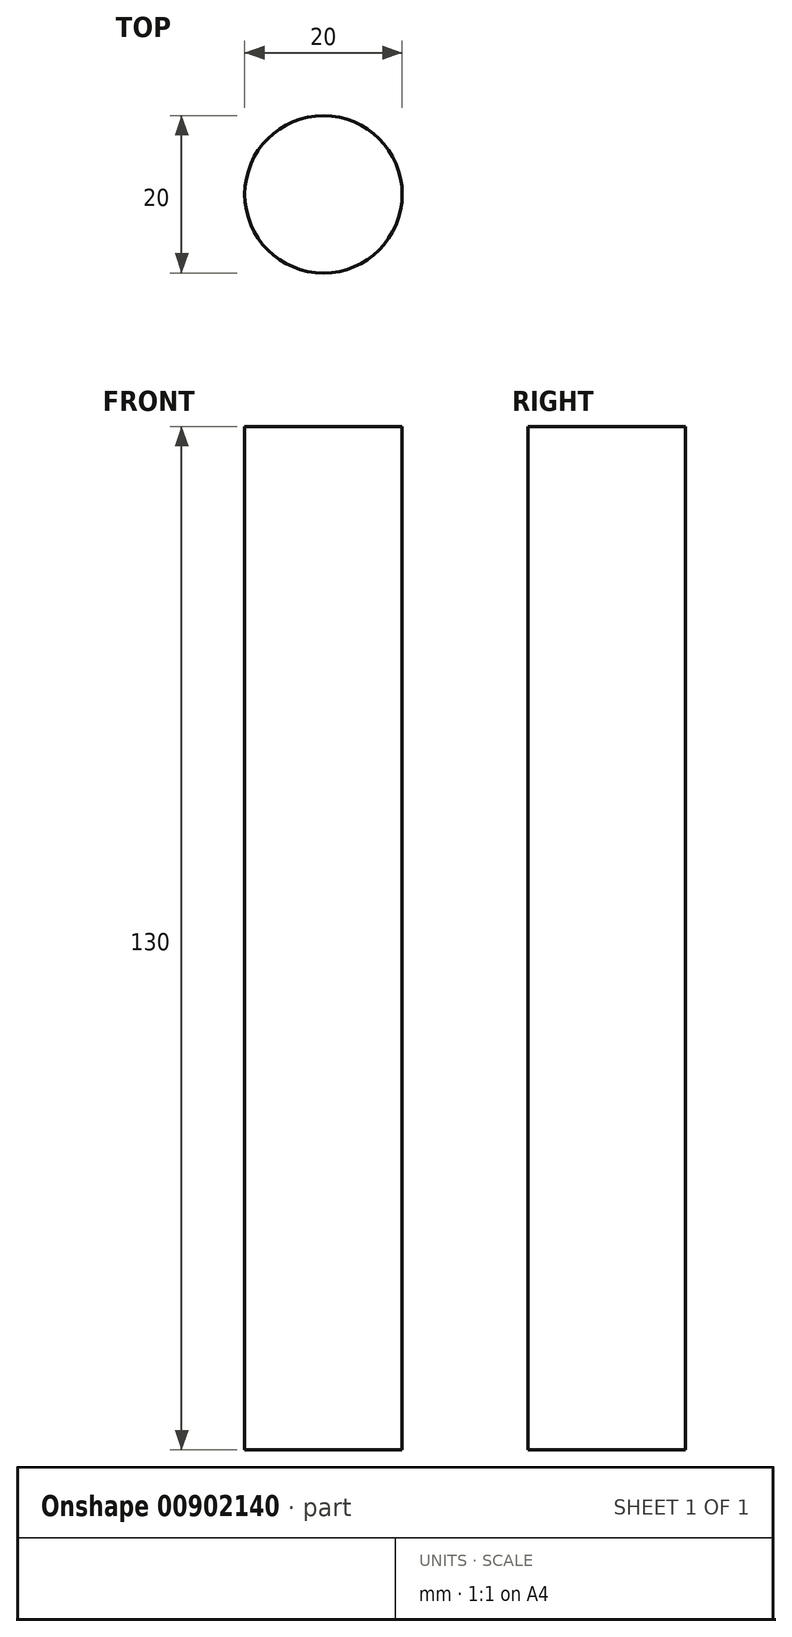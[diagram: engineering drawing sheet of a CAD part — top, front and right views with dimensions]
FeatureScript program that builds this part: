
annotation { "Feature Type Name" : "Feature", "Feature Type Description" : "" }
export const myFeature = defineFeature(function(context is Context, id is Id, definition is map)
    precondition{}
    {
        {
            var Q0;
            Q0=qCreatedBy(makeId("Top.planeOp"),FACE);
            var sketch = newSketch(context, id + "F0", { "sketchPlane" : qUnion([Q0])});
            skCircle(sketch, "E0", {"center": v(0, 0) * mm, "radius": 10 * mm});
            skSolve(sketch);
        }
        {
            var Q0;
            Q0 = qSketchRegion(id + "F0", true);
            extrude(context, id + "F1", {"entities" : qUnion([Q0]), "depth" : 130 * mm, "offsetDistance" : 25 * mm});
        }
    });
